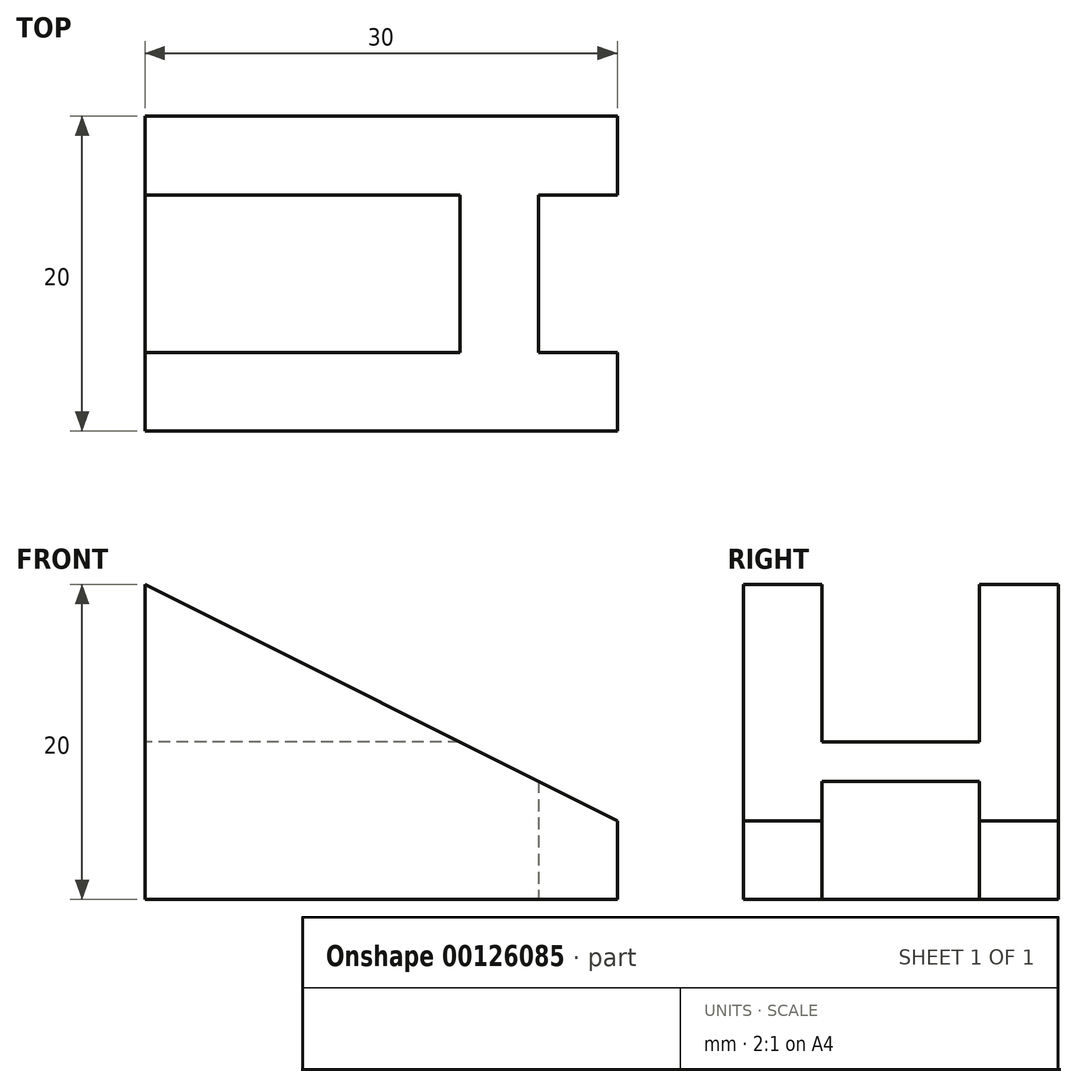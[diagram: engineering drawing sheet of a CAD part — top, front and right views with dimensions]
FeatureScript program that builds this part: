
annotation { "Feature Type Name" : "Feature", "Feature Type Description" : "" }
export const myFeature = defineFeature(function(context is Context, id is Id, definition is map)
    precondition{}
    {
        {
            var Q0;
            Q0=qCreatedBy(makeId("Front.planeOp"),FACE);
            var sketch = newSketch(context, id + "F0", { "sketchPlane" : qUnion([Q0])});
            skLineSegment(sketch, "E0", {"start": v(0, 0) * mm, "end": v(30, 0) * mm});
            skLineSegment(sketch, "E1", {"start": v(30, 0) * mm, "end": v(30, 5) * mm});
            skLineSegment(sketch, "E2", {"start": v(30, 5) * mm, "end": v(0, 20) * mm});
            skLineSegment(sketch, "E3", {"start": v(0, 20) * mm, "end": v(0, 0) * mm});
            skSolve(sketch);
        }
        {
            var Q0;
            Q0 = qSketchRegion(id + "F0", true);
            extrude(context, id + "F1", {"entities" : qUnion([Q0]), "endBound" : BoundingType.SYMMETRIC, "depth" : 20 * mm});
        }
        {
            var Q0;
            Q0=makeQuery(id+"F1.opExtrude","SWEPT_FACE",FACE,{"disambiguationData":[OSD([sQuery(id+"F0.wireOp",EDGE,"E3")])]});
            var sketch = newSketch(context, id + "F2", { "sketchPlane" : qUnion([Q0])});
            skLineSegment(sketch, "E4.bottom", {"start": v(5, 10) * mm, "end": v(-5, 10) * mm});
            skLineSegment(sketch, "E4.top", {"start": v(5, 30) * mm, "end": v(-5, 30) * mm});
            skLineSegment(sketch, "E4.left", {"start": v(5, 10) * mm, "end": v(5, 30) * mm});
            skLineSegment(sketch, "E4.right", {"start": v(-5, 10) * mm, "end": v(-5, 30) * mm});
            skPoint(sketch, "E4.middle", {"position": v(0, 20) * mm});
            skSolve(sketch);
        }
        {
            var Q0;
            Q0 = qSketchRegion(id + "F2", true);
            var Q1;
            Q1=makeQuery(id+"F1.opExtrude","SWEPT_FACE",FACE,{"disambiguationData":[OSD([sQuery(id+"F0.wireOp",EDGE,"E2")])]});
            extrude(context, id + "F3", {"entities" : qUnion([Q0]), "operationType" : NewBodyOperationType.REMOVE, "endBound" : BoundingType.UP_TO_SURFACE, "oppositeDirection" : true, "endBoundEntityFace" : qUnion([Q1]), "depth" : 25 * mm});
        }
        {
            var Q0;
            Q0=makeQuery(id+"F1.opExtrude","SWEPT_FACE",FACE,{"disambiguationData":[OSD([sQuery(id+"F0.wireOp",EDGE,"E0")])]});
            var sketch = newSketch(context, id + "F4", { "sketchPlane" : qUnion([Q0])});
            skLineSegment(sketch, "E5.bottom", {"start": v(35, -5) * mm, "end": v(25, -5) * mm});
            skLineSegment(sketch, "E5.top", {"start": v(35, 5) * mm, "end": v(25, 5) * mm});
            skLineSegment(sketch, "E5.left", {"start": v(35, -5) * mm, "end": v(35, 5) * mm});
            skLineSegment(sketch, "E5.right", {"start": v(25, -5) * mm, "end": v(25, 5) * mm});
            skPoint(sketch, "E5.middle", {"position": v(30, 0) * mm});
            skSolve(sketch);
        }
        {
            var Q0;
            Q0 = qSketchRegion(id + "F4", true);
            var Q1;
            Q1=makeQuery(id+"F1.opExtrude","SWEPT_FACE",FACE,{"disambiguationData":[OSD([sQuery(id+"F0.wireOp",EDGE,"E2")])]});
            extrude(context, id + "F5", {"entities" : qUnion([Q0]), "operationType" : NewBodyOperationType.REMOVE, "endBound" : BoundingType.UP_TO_SURFACE, "oppositeDirection" : true, "endBoundEntityFace" : qUnion([Q1]), "depth" : 25 * mm});
        }
    });
